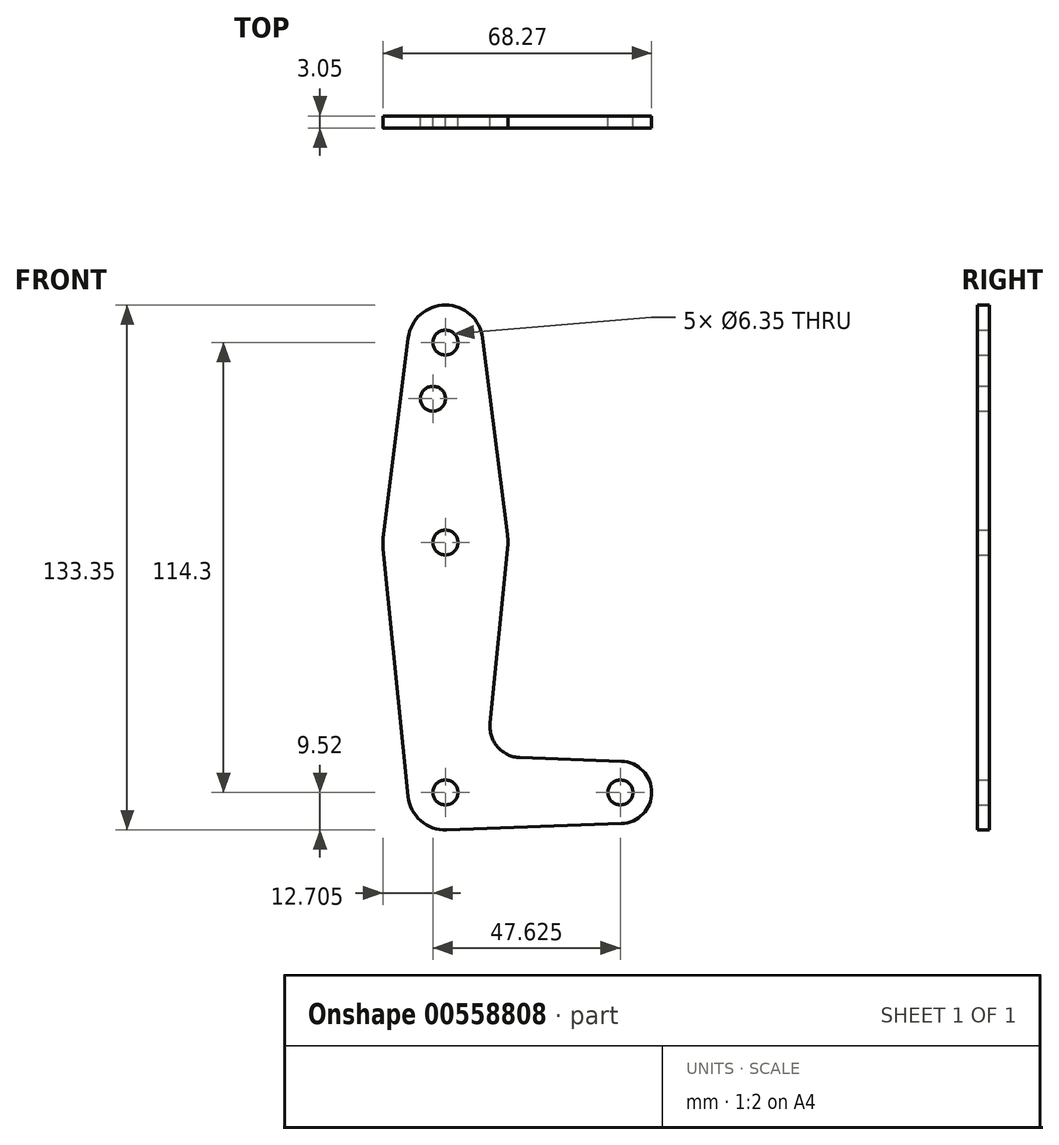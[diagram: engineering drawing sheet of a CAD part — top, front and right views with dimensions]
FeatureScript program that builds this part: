
annotation { "Feature Type Name" : "Feature", "Feature Type Description" : "" }
export const myFeature = defineFeature(function(context is Context, id is Id, definition is map)
    precondition{}
    {
        {
            var Q0;
            Q0=qCreatedBy(makeId("Front.planeOp"),FACE);
            var sketch = newSketch(context, id + "F0", { "sketchPlane" : qUnion([Q0])});
            skCircle(sketch, "E0", {"center": v(0, 114.3) * mm, "radius": 9.53 * mm});
            skCircle(sketch, "E1", {"center": v(0, 63.5) * mm, "radius": 15.88 * mm});
            skCircle(sketch, "E2", {"center": v(0, 0) * mm, "radius": 9.53 * mm});
            skCircle(sketch, "E3", {"center": v(44.45, 0) * mm, "radius": 7.94 * mm});
            skLineSegment(sketch, "E4", {"start": v(0, 114.3) * mm, "end": v(0, 0) * mm, "construction": true});
            skLineSegment(sketch, "E5", {"start": v(44.45, 0) * mm, "end": v(0, 0) * mm, "construction": true});
            skLineSegment(sketch, "E6", {"start": v(-9.48, -0.95) * mm, "end": v(-15.8, 61.91) * mm});
            skLineSegment(sketch, "E7", {"start": v(-15.75, 65.48) * mm, "end": v(-9.45, 115.5) * mm});
            skLineSegment(sketch, "E8", {"start": v(9.45, 115.5) * mm, "end": v(15.75, 65.48) * mm});
            skLineSegment(sketch, "E9", {"start": v(15.8, 61.91) * mm, "end": v(11.34, 17.6) * mm});
            skLineSegment(sketch, "E10", {"start": v(44.73, 7.93) * mm, "end": v(18.97, 8.85) * mm});
            skLineSegment(sketch, "E11", {"start": v(44.73, -7.93) * mm, "end": v(0.34, -9.52) * mm});
            skCircle(sketch, "E12", {"center": v(0, 114.3) * mm, "radius": 3.18 * mm});
            skCircle(sketch, "E13", {"center": v(-3.17, 100.03) * mm, "radius": 3.18 * mm});
            skCircle(sketch, "E14", {"center": v(0, 63.5) * mm, "radius": 3.18 * mm});
            skCircle(sketch, "E15", {"center": v(0, 0) * mm, "radius": 3.18 * mm});
            skCircle(sketch, "E16", {"center": v(44.45, 0) * mm, "radius": 3.18 * mm});
            skArc(sketch, "E17.filletArc", {"start": v(11.34, 17.6) * mm, "mid": v(13.26, 11.57) * mm, "end": v(18.97, 8.85) * mm});
            skSolve(sketch);
        }
        {
            var Q0;
            Q0=makeQuery(id+"F0.imprint","IMPRINT",FACE,{"disambiguationData":[TD([[makeQuery(id+"F0.imprint","IMPRINT",EDGE,{"derivedFrom":sQuery(id+"F0.wireOp",EDGE,"E12")}),-1.0]])]});
            var Q1;
            {var subQ1=sQuery(id+"F0.wireOp",EDGE,"E7");Q1=makeQuery(id+"F0.imprint","IMPRINT",FACE,{"disambiguationData":[TD([[makeQuery(id+"F0.imprint","IMPRINT",EDGE,{"derivedFrom":subQ1}),-1.0]])]});}
            var Q2;
            Q2=makeQuery(id+"F0.imprint","IMPRINT",FACE,{"disambiguationData":[TD([[makeQuery(id+"F0.imprint","IMPRINT",EDGE,{"derivedFrom":sQuery(id+"F0.wireOp",EDGE,"E14")}),-1.0]])]});
            var Q3;
            {var subQ0=sQuery(id+"F0.wireOp",EDGE,"E6");Q3=makeQuery(id+"F0.imprint","IMPRINT",FACE,{"disambiguationData":[TD([[makeQuery(id+"F0.imprint","IMPRINT",EDGE,{"derivedFrom":subQ0}),-1.0]])]});}
            var Q4;
            Q4=makeQuery(id+"F0.imprint","IMPRINT",FACE,{"disambiguationData":[TD([[makeQuery(id+"F0.imprint","IMPRINT",EDGE,{"derivedFrom":sQuery(id+"F0.wireOp",EDGE,"E16")}),-1.0]])]});
            var Q5;
            Q5=makeQuery(id+"F0.imprint","IMPRINT",FACE,{"disambiguationData":[TD([[makeQuery(id+"F0.imprint","IMPRINT",EDGE,{"derivedFrom":sQuery(id+"F0.wireOp",EDGE,"E15")}),-1.0]])]});
            extrude(context, id + "F1", {"entities" : qUnion([Q0, Q1, Q2, Q3, Q4, Q5]), "depth" : 3.05 * mm, "offsetDistance" : 25.4 * mm});
        }
    });
